# Revit family: 1Electronics_Commercial-Audio_Biamp_Digital-Paging-Station_Dimic1_Dimic12_Dimic12S
name_source: partatom
category: Communication Devices
units: mm (PartAtom-declared; Revit-internal decimal feet)

## family parameters
Cut with Voids When Loaded = No
Host = Face
Maintain Annotation Orientation = No
OmniClass Number = 23.85.10.11.14.14.11
Part Type = Normal
Room Calculation Point = No
Round Connector Dimension = Use Diameter
Shared = No

## types (3) — shared parameters
Active = Yes
Apparent Load = 0 VA
Connector Description = 24 VDC jack
Current = 0.00075 A
Cut-out dimension in mm = 85 x 230
Default Elevation = 4' - 0"
Depth = 0' - 9 1/2"
Height = 0' - 2 1/2"
Housing Material = Biamp - Plastic - Dark Gray
Manufacturer = Biamp
Max Power Consumption = 0 W
Number of Poles = 1
Power Factor = 1
Product Documentation Link = https://downloads.biamp.com
Product Page URL = https://www.biamp.com
Product data url = https://www.bimobject.com
Supported main unit = AUDIOCONTROL12.8
URL = https://www.biamp.com
Voltage = 24 V
Width = 0' - 4 1/2"

## per-type parameters (varying)
| type | Button | Buttons | Cable length in m | Cable type | Description | Frequency range | Indicator | Lo-cut | Microphone | Nominal output level | Polar pattern | Power type | Weight | Zones |
| 1 | No | All zone selection button | 5 | CAT5 | DIMIC1 All Call Digital Paging Station for AUDIOCONTROL12.8 | 220 Hz - 20 kHz | Tri-color status | 220 Hz, 6dB/oct | Yes | 775mV variable balanced | Uni-directional | Phantom or external power supply | 1.32 lb |  |
| 12 | Yes | 12 programmable + Call + All Call | 5 | CAT5 | DIMIC12 Selective Programmable Digital Paging Station for AC12.8 | 220 Hz - 20 kHz | 1 per button + multi-color status | 220 Hz, 6dB/oct | Yes | 775mV variable balanced | Uni-directional | Phantom or external power supply | 1.50 lb | Up to 12 |
| 12S | Yes | 12 programmable |  |  | DIMIC12S DIMIC12 Extension for AUDIOCONTROL12.8 |  | 1 per button |  | No |  |  | Powered from DIMIC12 | 0.75 lb | 12 (up to 96) |

note: column(s) folded — value = type name in every type: Model

## geometry (parser evidence)
native form markers: Sweep x2
no freeform markers — native parametric forms only
